# Revit family: Bath-Freestanding-KOHLER-KARING-K-EX31162T_1
name_source: partatom
category: Plumbing Fixtures
units: mm (PartAtom-declared; Revit-internal decimal feet)

## family parameters
Cut with Voids When Loaded = No
Host = Face
Maintain Annotation Orientation = No
OmniClass Number = 23.31.15.00
OmniClass Title = Bathtubs
Part Type = Normal
Room Calculation Point = No
Round Connector Dimension = Use Diameter
Shared = No

## types (2) — shared parameters
ADA Compliant = No
Assembly Code = D2010500
CW Connection = No
Cold Water Inlet = Cold Water Inlet
Date Modified = 05/10/2022
Default Elevation = 0"
Drain Included = Yes
Finish = Kohler-Lithocast-0-White
HW Connection = No
Height = 23 13/16"
Hot Water Inlet = Hot Water Inlet
Length = 31 3/8"
Manufacturer = Kohler Co.
Master Format 2014 = 22 41 19
Master Format 2014 Name = Residential Bathtubs
Material = Lithocast
Product Name = KARING
URL = http://www.kohler.com.cn
Vent Connection = No
Waste Connection = Yes
Waste Water Outlet = Waste Water Outlet
WaterSense Certified = No
Width = 66 15/16"

## per-type parameters (varying)
| type | Description | Model | Type |
| 0-White | 1.7M KARING 2.0 GEL COAT LITHOCAST GLOSSY BATH | K-EX31162T-0 | 1 |
| MAT,0-White | 1.7M KARING 2.0 GEL COAT LITHOCAST BATH (MATTE) | K-EX31162T-MAT-0 | 2 |

## geometry (parser evidence)
native form markers: Sweep x4
no freeform markers — native parametric forms only
